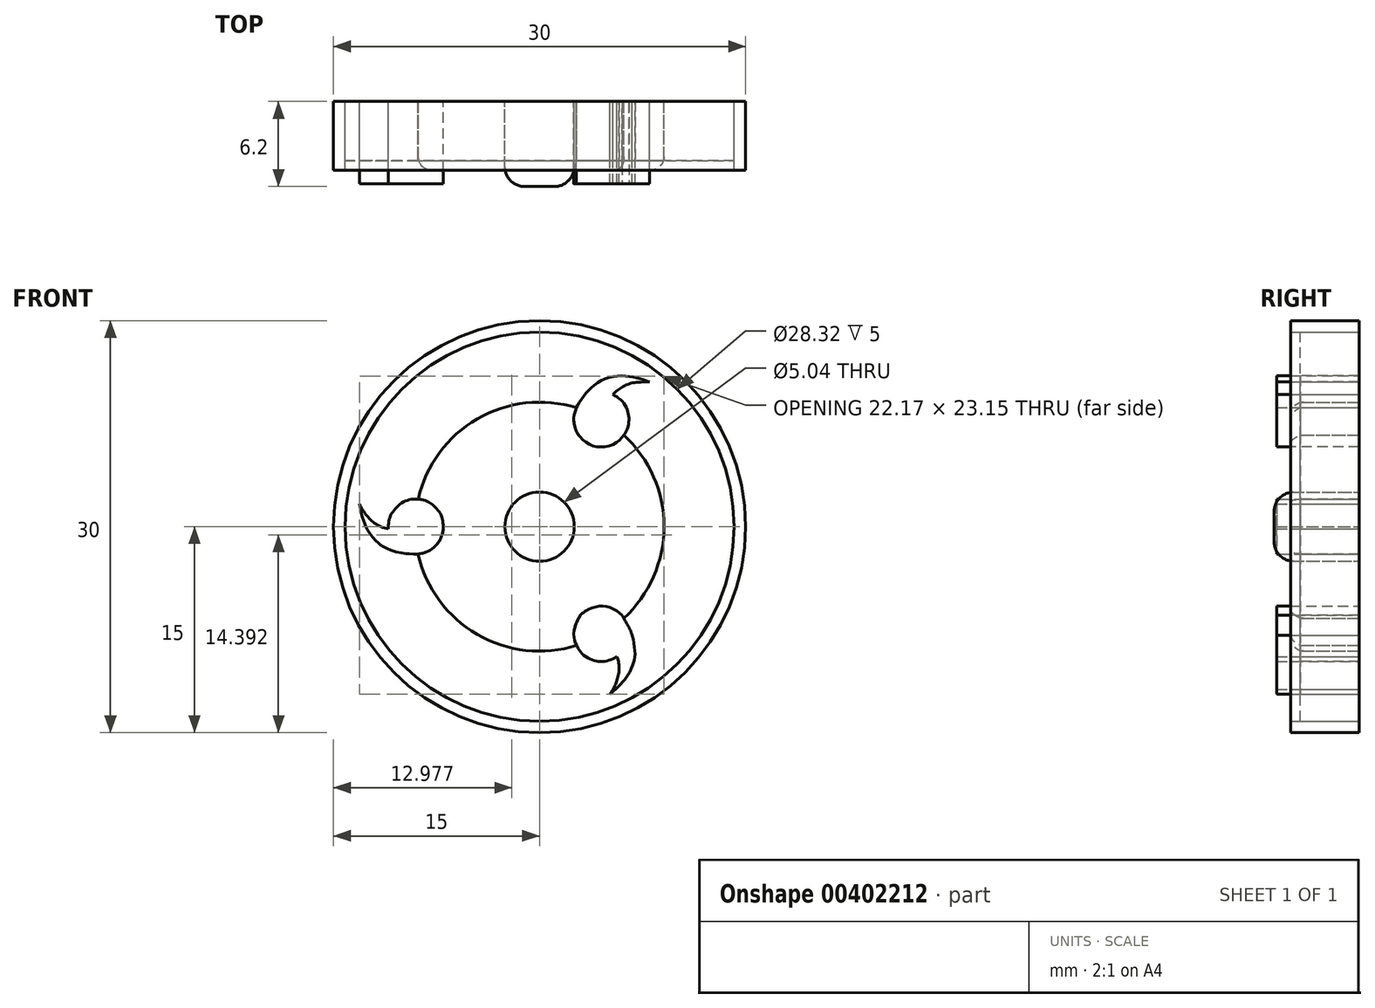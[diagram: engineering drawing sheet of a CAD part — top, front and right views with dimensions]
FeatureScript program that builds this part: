
annotation { "Feature Type Name" : "Feature", "Feature Type Description" : "" }
export const myFeature = defineFeature(function(context is Context, id is Id, definition is map)
    precondition{}
    {
        {
            var Q0;
            Q0=qCreatedBy(makeId("Front.planeOp"),FACE);
            var sketch = newSketch(context, id + "F0", { "sketchPlane" : qUnion([Q0])});
            skLineSegment(sketch, "E0", {"start": v(15, 30) * mm, "end": v(15, 0) * mm, "construction": true});
            skLineSegment(sketch, "E1", {"start": v(0, 15) * mm, "end": v(15, 15) * mm, "construction": true});
            skLineSegment(sketch, "E2", {"start": v(15, 15) * mm, "end": v(30, 15) * mm, "construction": true});
            skCircle(sketch, "E3", {"center": v(15, 15) * mm, "radius": 15 * mm});
            skCircle(sketch, "E4", {"center": v(15, 15) * mm, "radius": 14.16 * mm});
            skCircle(sketch, "E5", {"center": v(15, 15) * mm, "radius": 2.52 * mm});
            skCircle(sketch, "E6", {"center": v(15, 15) * mm, "radius": 9.06 * mm});
            skFitSpline(sketch, "E7", {"points": [v(8, 15) * mm, v(7.92, 15.63) * mm, v(7.7, 16.07) * mm, v(7.25, 16.56) * mm, v(6.8, 16.85) * mm, v(6.16, 17) * mm, v(5.52, 16.96) * mm, v(4.96, 16.73) * mm, v(4.5, 16.3) * mm, v(4.18, 15.85) * mm, v(4.03, 15.33) * mm, v(3.98, 14.83) * mm], "startDerivative": vector(-0.44, 7.05) * mm, "endDerivative": vector(-0.35, -5.83) * mm});
            skFitSpline(sketch, "E8", {"points": [v(3.98, 14.83) * mm, v(3.75, 14.9) * mm, v(3.45, 15) * mm, v(3.22, 15.11) * mm, v(3, 15.25) * mm, v(2.8, 15.4) * mm, v(2.64, 15.55) * mm, v(2.5, 15.7) * mm, v(2.34, 15.9) * mm, v(2.2, 16.09) * mm, v(2.12, 16.22) * mm, v(2.04, 16.36) * mm, v(1.96, 16.5) * mm, v(1.9, 16.66) * mm], "startDerivative": vector(-2.74, 0.66) * mm, "endDerivative": vector(-1, 2.3) * mm});
            skFitSpline(sketch, "E9", {"points": [v(1.9, 16.66) * mm, v(1.9, 16.5) * mm, v(1.93, 16.4) * mm, v(1.95, 16.26) * mm, v(2, 16.08) * mm, v(2.06, 15.83) * mm, v(2.1, 15.67) * mm, v(2.17, 15.48) * mm, v(2.25, 15.25) * mm, v(2.31, 15.1) * mm, v(2.38, 14.96) * mm, v(2.48, 14.77) * mm, v(2.58, 14.6) * mm, v(2.65, 14.49) * mm, v(2.75, 14.34) * mm, v(2.87, 14.2) * mm, v(3.02, 14.03) * mm, v(3.2, 13.87) * mm, v(3.3, 13.78) * mm, v(3.43, 13.68) * mm, v(3.6, 13.56) * mm, v(3.83, 13.44) * mm, v(4.05, 13.34) * mm, v(4.44, 13.2) * mm, v(4.9, 13.1) * mm, v(5.27, 13.04) * mm, v(5.45, 13.02) * mm, v(5.7, 13.01) * mm, v(6.01, 13) * mm, v(6.35, 13.03) * mm, v(6.78, 13.17) * mm, v(7.13, 13.36) * mm, v(7.45, 13.63) * mm, v(7.6, 13.82) * mm, v(7.77, 14.08) * mm, v(7.9, 14.39) * mm, v(7.96, 14.6) * mm, v(7.98, 14.75) * mm, v(8, 14.92) * mm, v(8, 15) * mm], "startDerivative": vector(0.41, -7.75) * mm, "endDerivative": vector(-0.48, 4.5) * mm});
            skFitSpline(sketch, "E10", {"points": [v(20.34, 24.6) * mm, v(20.44, 24.72) * mm, v(20.61, 24.88) * mm, v(20.83, 25.04) * mm, v(21, 25.15) * mm, v(21.22, 25.27) * mm, v(21.4, 25.34) * mm, v(21.62, 25.43) * mm, v(21.9, 25.48) * mm, v(22.2, 25.5) * mm, v(22.52, 25.53) * mm, v(22.8, 25.53) * mm, v(23, 25.54) * mm], "startDerivative": vector(1.4, 1.67) * mm, "endDerivative": vector(2.45, 0.12) * mm});
            skFitSpline(sketch, "E11", {"points": [v(23, 25.54) * mm, v(22.74, 25.63) * mm, v(22.5, 25.7) * mm, v(22.17, 25.8) * mm, v(21.78, 25.89) * mm, v(21.36, 25.96) * mm, v(20.9, 25.97) * mm, v(20.42, 25.94) * mm, v(19.9, 25.8) * mm, v(19.46, 25.62) * mm, v(19.04, 25.34) * mm, v(18.73, 25.07) * mm, v(18.43, 24.76) * mm, v(18.2, 24.45) * mm, v(17.97, 24.13) * mm, v(17.8, 23.87) * mm, v(17.68, 23.65) * mm], "startDerivative": vector(-4.94, 1.9) * mm, "endDerivative": vector(-1.48, -4.44) * mm});
            skFitSpline(sketch, "E12", {"points": [v(20.34, 24.6) * mm, v(20.66, 24.42) * mm, v(20.88, 24.26) * mm, v(21.1, 24.02) * mm, v(21.35, 23.58) * mm, v(21.45, 23.25) * mm, v(21.5, 22.88) * mm, v(21.48, 22.52) * mm, v(21.39, 22.11) * mm, v(21.22, 21.8) * mm, v(21.14, 21.66) * mm, v(20.9, 21.38) * mm, v(20.63, 21.16) * mm, v(20.17, 20.9) * mm, v(19.63, 20.8) * mm, v(19.16, 20.82) * mm, v(18.68, 20.97) * mm, v(18.32, 21.2) * mm, v(17.95, 21.53) * mm, v(17.69, 21.93) * mm, v(17.57, 22.3) * mm, v(17.5, 22.6) * mm, v(17.5, 22.84) * mm, v(17.52, 23.1) * mm, v(17.57, 23.34) * mm, v(17.64, 23.53) * mm, v(17.68, 23.65) * mm], "startDerivative": vector(8.65, -4.8) * mm, "endDerivative": vector(1.07, 5.1) * mm});
            skFitSpline(sketch, "E13", {"points": [v(20.13, 2.82) * mm, v(20.18, 2.86) * mm, v(20.3, 2.97) * mm, v(20.46, 3.1) * mm, v(20.65, 3.27) * mm, v(20.84, 3.46) * mm, v(21.08, 3.73) * mm, v(21.33, 4.05) * mm, v(21.6, 4.49) * mm, v(21.8, 4.99) * mm, v(21.9, 5.3) * mm, v(21.95, 5.77) * mm, v(21.9, 6.36) * mm, v(21.74, 7.08) * mm], "startDerivative": vector(1.48, 1.12) * mm, "endDerivative": vector(-2.47, 6.66) * mm});
            skFitSpline(sketch, "E14", {"points": [v(21.74, 7.08) * mm, v(21.58, 7.54) * mm, v(21.35, 7.97) * mm, v(21, 8.56) * mm], "startDerivative": vector(-0.47, 1.5) * mm, "endDerivative": vector(-0.9, 1.72) * mm});
            skFitSpline(sketch, "E15", {"points": [v(21, 8.56) * mm, v(20.61, 8.9) * mm, v(20, 9.15) * mm, v(19.48, 9.22) * mm, v(18.87, 9.1) * mm, v(18.4, 8.88) * mm, v(17.98, 8.56) * mm, v(17.72, 8.07) * mm, v(17.55, 7.61) * mm, v(17.49, 7.08) * mm, v(17.57, 6.67) * mm, v(17.7, 6.35) * mm, v(17.85, 6.08) * mm, v(18.18, 5.69) * mm, v(18.67, 5.37) * mm, v(19.13, 5.23) * mm, v(19.58, 5.18) * mm, v(20.05, 5.28) * mm, v(20.46, 5.45) * mm, v(20.64, 5.55) * mm], "startDerivative": vector(-6.5, 6.38) * mm, "endDerivative": vector(4.57, 2.83) * mm});
            skFitSpline(sketch, "E16", {"points": [v(20.64, 5.55) * mm, v(20.74, 5.24) * mm, v(20.78, 4.8) * mm, v(20.77, 4.37) * mm, v(20.64, 3.85) * mm, v(20.5, 3.44) * mm, v(20.34, 3.16) * mm], "startDerivative": vector(0.81, -1.97) * mm, "endDerivative": vector(-1.32, -2.16) * mm});
            skFitSpline(sketch, "E17", {"points": [v(20.34, 3.16) * mm, v(20.29, 3.07) * mm, v(20.22, 2.97) * mm, v(20.13, 2.82) * mm], "startDerivative": vector(-0.16, -0.32) * mm, "endDerivative": vector(-0.25, -0.42) * mm});
            skSolve(sketch);
        }
        {
            var Q0;
            Q0=makeQuery(id+"F0.imprint","IMPRINT",FACE,{"disambiguationData":[TD([[makeQuery(id+"F0.imprint","IMPRINT",EDGE,{"derivedFrom":sQuery(id+"F0.wireOp",EDGE,"E3")}),1.0]])]});
            var Q1;
            Q1=makeQuery(id+"F0.imprint","IMPRINT",FACE,{"disambiguationData":[TD([[makeQuery(id+"F0.imprint","IMPRINT",EDGE,{"derivedFrom":sQuery(id+"F0.wireOp",EDGE,"E5")}),-1.0]])]});
            extrude(context, id + "F1", {"entities" : qUnion([Q0, Q1]), "depth" : 5 * mm});
        }
        {
            var Q0;
            {var subQ0=sQuery(id+"F0.wireOp",EDGE,"E12");var subQ1=sQuery(id+"F0.wireOp",EDGE,"E6");var subQ3=makeQuery(id+"F0.imprint","INTERSECT",VERTEX,{"derivedFrom":[subQ1,subQ0]});Q0=makeQuery(id+"F0.imprint","IMPRINT",FACE,{"disambiguationData":[TD([[makeQuery(id+"F0.imprint","IMPRINT",EDGE,{"disambiguationData":[TD([[subQ3,-1.0]])],"derivedFrom":subQ1}),1.0]])]});}
            var Q1;
            {var subQ4=sQuery(id+"F0.wireOp",EDGE,"E10");Q1=makeQuery(id+"F0.imprint","IMPRINT",FACE,{"disambiguationData":[TD([[makeQuery(id+"F0.imprint","IMPRINT",EDGE,{"derivedFrom":subQ4}),1.0]])]});}
            var Q2;
            {var subQ0=sQuery(id+"F0.wireOp",EDGE,"E15");var subQ1=sQuery(id+"F0.wireOp",EDGE,"E6");var subQ2=makeQuery(id+"F0.imprint","INTERSECT",VERTEX,{"derivedFrom":[subQ1,subQ0]});Q2=makeQuery(id+"F0.imprint","IMPRINT",FACE,{"disambiguationData":[TD([[makeQuery(id+"F0.imprint","IMPRINT",EDGE,{"disambiguationData":[TD([[subQ2,-1.0]])],"derivedFrom":subQ1}),1.0]])]});}
            var Q3;
            {var subQ1=sQuery(id+"F0.wireOp",EDGE,"E13");Q3=makeQuery(id+"F0.imprint","IMPRINT",FACE,{"disambiguationData":[TD([[makeQuery(id+"F0.imprint","IMPRINT",EDGE,{"derivedFrom":subQ1}),1.0]])]});}
            var Q4;
            {var subQ5=sQuery(id+"F0.wireOp",EDGE,"E8");Q4=makeQuery(id+"F0.imprint","IMPRINT",FACE,{"disambiguationData":[TD([[makeQuery(id+"F0.imprint","IMPRINT",EDGE,{"derivedFrom":subQ5}),1.0]])]});}
            var Q5;
            {var subQ0=sQuery(id+"F0.wireOp",EDGE,"E7");var subQ1=sQuery(id+"F0.wireOp",EDGE,"E6");var subQ2=makeQuery(id+"F0.imprint","INTERSECT",VERTEX,{"derivedFrom":[subQ1,subQ0]});Q5=makeQuery(id+"F0.imprint","IMPRINT",FACE,{"disambiguationData":[TD([[makeQuery(id+"F0.imprint","IMPRINT",EDGE,{"disambiguationData":[TD([[subQ2,-1.0]])],"derivedFrom":subQ1}),1.0]])]});}
            extrude(context, id + "F2", {"entities" : qUnion([Q0, Q1, Q2, Q3, Q4, Q5]), "depth" : 6 * mm});
        }
        {
            var Q0;
            Q0=makeQuery(id+"F0.imprint","IMPRINT",FACE,{"disambiguationData":[TD([[makeQuery(id+"F0.imprint","IMPRINT",EDGE,{"derivedFrom":sQuery(id+"F0.wireOp",EDGE,"E5")}),1.0]])]});
            extrude(context, id + "F3", {"entities" : qUnion([Q0]), "depth" : 6.2 * mm});
        }
        {
            var Q0;
            Q0=makeQuery(id+"F0.imprint","IMPRINT",FACE,{"disambiguationData":[TD([[makeQuery(id+"F0.imprint","IMPRINT",EDGE,{"derivedFrom":sQuery(id+"F0.wireOp",EDGE,"E4")}),1.0]])]});
            extrude(context, id + "F4", {"entities" : qUnion([Q0]), "depth" : 4.3 * mm});
        }
        {
            var Q0;
            {var subQ0=sQuery(id+"F0.wireOp",EDGE,"E6");Q0=makeQuery(id+"F1.opExtrude","CAP_EDGE",EDGE,{"disambiguationData":[OSD([subQ0]),TDD([makeQuery(id+"F0.imprint","IMPRINT",EDGE,{"disambiguationData":[TD([[makeQuery(id+"F0.imprint","INTERSECT",VERTEX,{"derivedFrom":[subQ0,sQuery(id+"F0.wireOp",EDGE,"E12")]}),1.0]])],"derivedFrom":subQ0})])],"isStart":false});}
            var Q1;
            {var subQ0=sQuery(id+"F0.wireOp",EDGE,"E6");Q1=makeQuery(id+"F1.opExtrude","CAP_EDGE",EDGE,{"disambiguationData":[OSD([subQ0]),TDD([makeQuery(id+"F0.imprint","IMPRINT",EDGE,{"disambiguationData":[TD([[makeQuery(id+"F0.imprint","INTERSECT",VERTEX,{"derivedFrom":[subQ0,sQuery(id+"F0.wireOp",EDGE,"E7")]}),1.0]])],"derivedFrom":subQ0})])],"isStart":false});}
            var Q2;
            {var subQ0=sQuery(id+"F0.wireOp",EDGE,"E6");Q2=makeQuery(id+"F1.opExtrude","CAP_EDGE",EDGE,{"disambiguationData":[OSD([subQ0]),TDD([makeQuery(id+"F0.imprint","IMPRINT",EDGE,{"disambiguationData":[TD([[makeQuery(id+"F0.imprint","INTERSECT",VERTEX,{"derivedFrom":[subQ0,sQuery(id+"F0.wireOp",EDGE,"E9")]}),-1.0]])],"derivedFrom":subQ0})])],"isStart":false});}
            fillet(context, id + "F5", {"entities" : qUnion([Q0, Q1, Q2]), "radius" : 0.97 * mm, "tangentPropagation" : true, "allowEdgeOverflow" : false});
        }
        {
            var Q0;
            Q0=makeQuery(id+"F3.opExtrude","CAP_EDGE",EDGE,{"disambiguationData":[OSD([sQuery(id+"F0.wireOp",EDGE,"E5")])],"isStart":false});
            fillet(context, id + "F6", {"entities" : qUnion([Q0]), "radius" : 1.45 * mm, "tangentPropagation" : true, "allowEdgeOverflow" : false});
        }
    });
